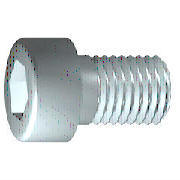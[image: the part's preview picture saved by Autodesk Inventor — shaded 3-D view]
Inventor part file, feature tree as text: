
AUTODESK INVENTOR PART (.ipt)
format: ipt  version: 2022 (Build 260153000, 153)  size: 199,168 bytes
history: native  units: mm (DEFAULTED — no unit token found)
features: sketch x2, other x1, extrude x1, plane x1, fillet x1
ambient origin geometry x7: Origin, YZ Plane, XY Plane, X Axis, Y Axis, Z Axis, Center Point
bodies: Solid1 (feature_tree)
feature tree (6):
  other  "Cuerpo"
  extrude  "Ranura"  Depth=2.0mm
  plane  "Work Plane1"
  fillet  "Fillet2"  Radius=2.0mm
  sketch  "Boceto1"  dims[d1=3.0mm d2=0.24548mm d3=2.0mm]
  sketch  "Boceto2"  dims[d4=1.0mm d5=60.0deg d6=2.0mm d7=2.0mm d8=1.732051mm d9=3.8mm d10=90.0deg d11=10.0mm d12=0.0mm d13=3.0mm d14=0.0mm d15=0.24538mm d16=0.24538mm d17=0.2mm d19=0.0mm d26=4.0mm d27=45.0deg d28=0.0mm d29=0.0mm d30=0.1mm]
